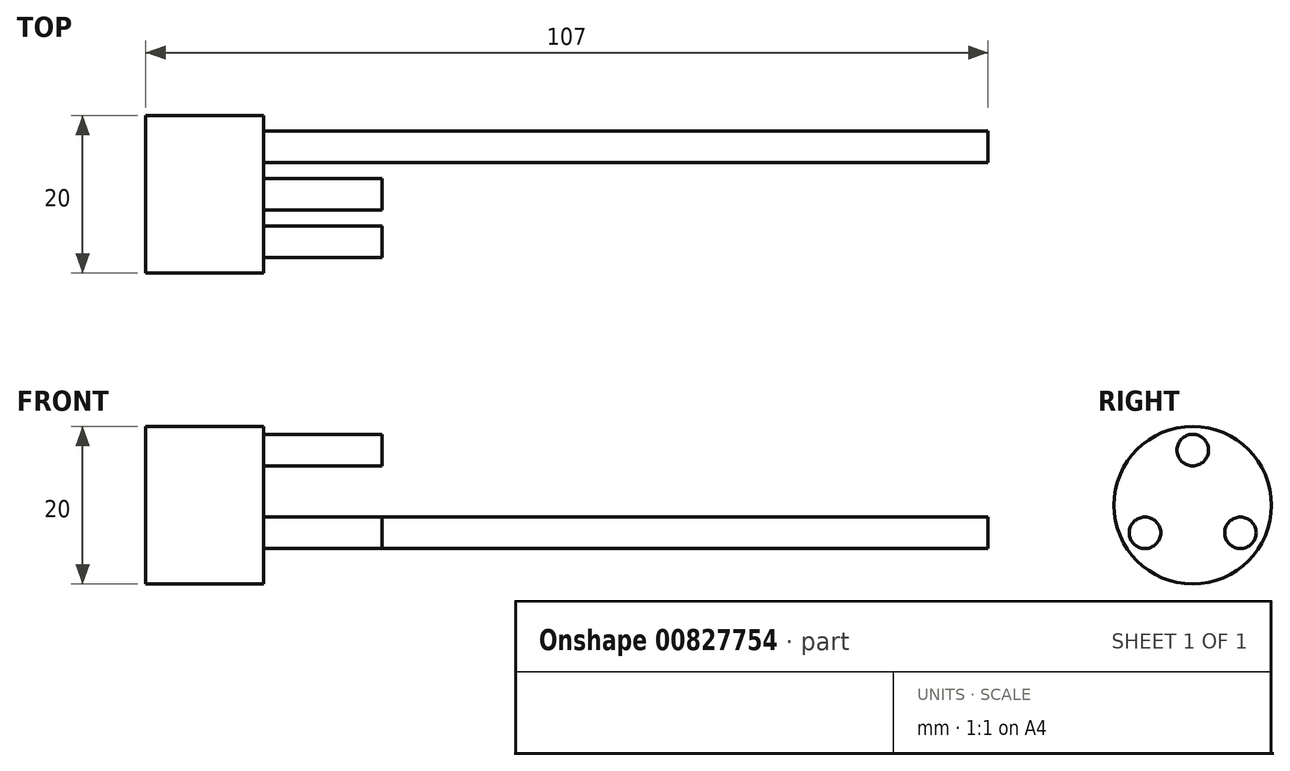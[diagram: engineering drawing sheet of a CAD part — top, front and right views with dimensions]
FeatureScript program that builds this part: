
annotation { "Feature Type Name" : "Feature", "Feature Type Description" : "" }
export const myFeature = defineFeature(function(context is Context, id is Id, definition is map)
    precondition{}
    {
        {
            var Q0;
            Q0=qCreatedBy(makeId("Right.planeOp"),FACE);
            var sketch = newSketch(context, id + "F0", { "sketchPlane" : qUnion([Q0])});
            skCircle(sketch, "E0", {"center": v(0, 0) * mm, "radius": 10 * mm});
            skLineSegment(sketch, "E1", {"start": v(0, 0) * mm, "end": v(10, 0) * mm});
            skSolve(sketch);
        }
        {
            var Q0;
            Q0=qSketchRegion(id+"F0",true);
            extrude(context, id + "F1", {"entities" : qUnion([Q0]), "depth" : 15 * mm});
        }
        {
            var Q0;
            Q0=makeQuery(id+"F1.opExtrude","CAP_FACE",FACE,{"disambiguationData":[OSD([sQuery(id+"F0.wireOp",EDGE,"E0")])],"isStart":false});
            var sketch = newSketch(context, id + "F2", { "sketchPlane" : qUnion([Q0])});
            skLineSegment(sketch, "E2", {"start": v(0, 5) * mm, "end": v(0, 7) * mm});
            skCircle(sketch, "E3", {"center": v(0, 7) * mm, "radius": 2 * mm});
            skLineSegment(sketch, "E4", {"start": v(0, 7) * mm, "end": v(2, 7) * mm});
            skCircle(sketch, "E5", {"center": v(6.06, -3.5) * mm, "radius": 2 * mm});
            skCircle(sketch, "E6", {"center": v(-6.06, -3.5) * mm, "radius": 2 * mm});
            skSolve(sketch);
        }
        {
            var Q0;
            Q0=qSketchRegion(id+"F2",true);
            extrude(context, id + "F3", {"entities" : qUnion([Q0]), "operationType" : NewBodyOperationType.ADD, "depth" : 15 * mm});
        }
        {
            var Q0;
            Q0=makeQuery(id+"F3.opExtrude","CAP_FACE",FACE,{"disambiguationData":[OSD([sQuery(id+"F2.wireOp",EDGE,"E5")])],"isStart":false});
            extrude(context, id + "F4", {"entities" : qUnion([Q0]), "operationType" : NewBodyOperationType.ADD, "depth" : 77 * mm, "offsetDistance" : 25 * mm});
        }
    });
